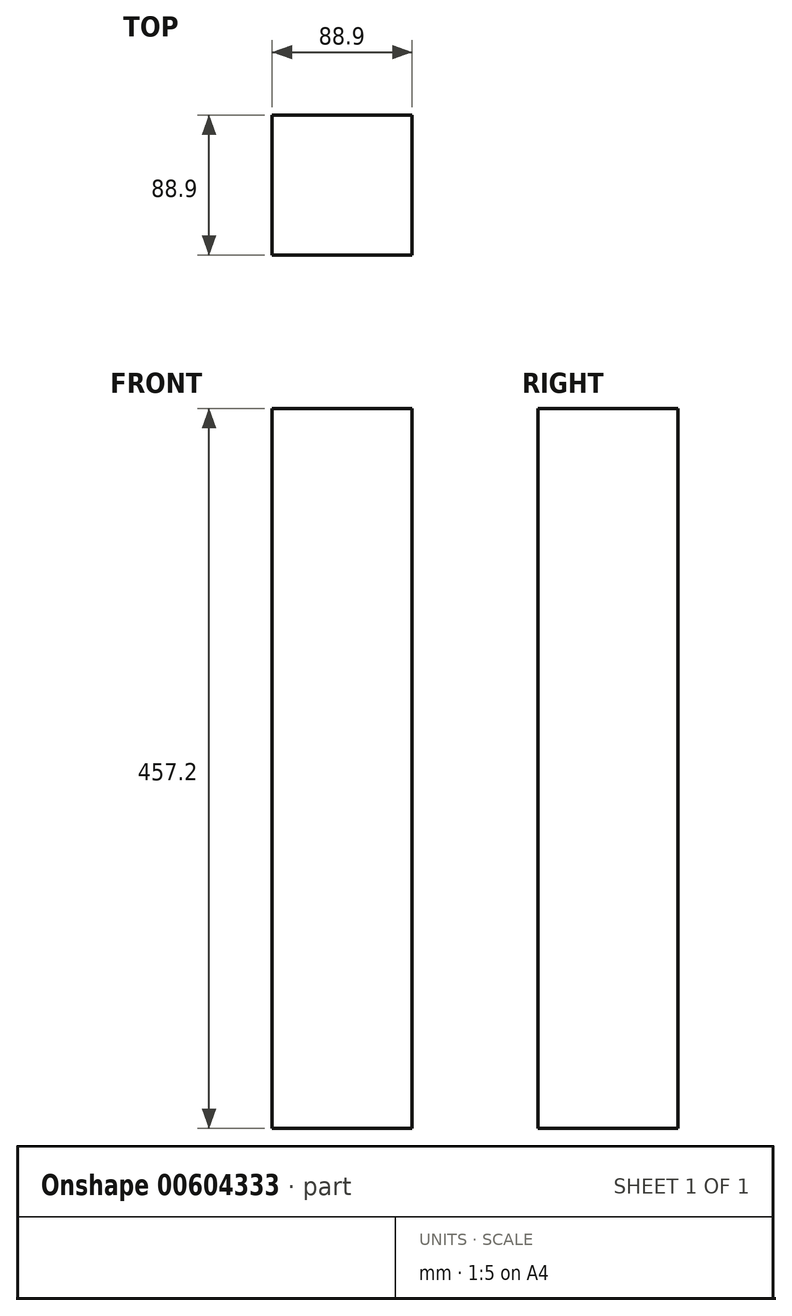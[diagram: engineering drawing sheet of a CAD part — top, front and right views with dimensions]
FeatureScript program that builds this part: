
annotation { "Feature Type Name" : "Feature", "Feature Type Description" : "" }
export const myFeature = defineFeature(function(context is Context, id is Id, definition is map)
    precondition{}
    {
        {
            var Q0;
            Q0=qCreatedBy(makeId("Top.planeOp"),FACE);
            var sketch = newSketch(context, id + "F0", { "sketchPlane" : qUnion([Q0])});
            skLineSegment(sketch, "E0.bottom", {"start": v(-44.45, -44.45) * mm, "end": v(44.45, -44.45) * mm});
            skLineSegment(sketch, "E0.top", {"start": v(-44.45, 44.45) * mm, "end": v(44.45, 44.45) * mm});
            skLineSegment(sketch, "E0.left", {"start": v(-44.45, -44.45) * mm, "end": v(-44.45, 44.45) * mm});
            skLineSegment(sketch, "E0.right", {"start": v(44.45, -44.45) * mm, "end": v(44.45, 44.45) * mm});
            skPoint(sketch, "E0.middle", {"position": v(0, 0) * mm});
            skSolve(sketch);
        }
        {
            var Q0;
            Q0 = qSketchRegion(id + "F0", true);
            extrude(context, id + "F1", {"entities" : qUnion([Q0]), "depth" : 457.2 * mm, "offsetDistance" : 25.4 * mm});
        }
    });
